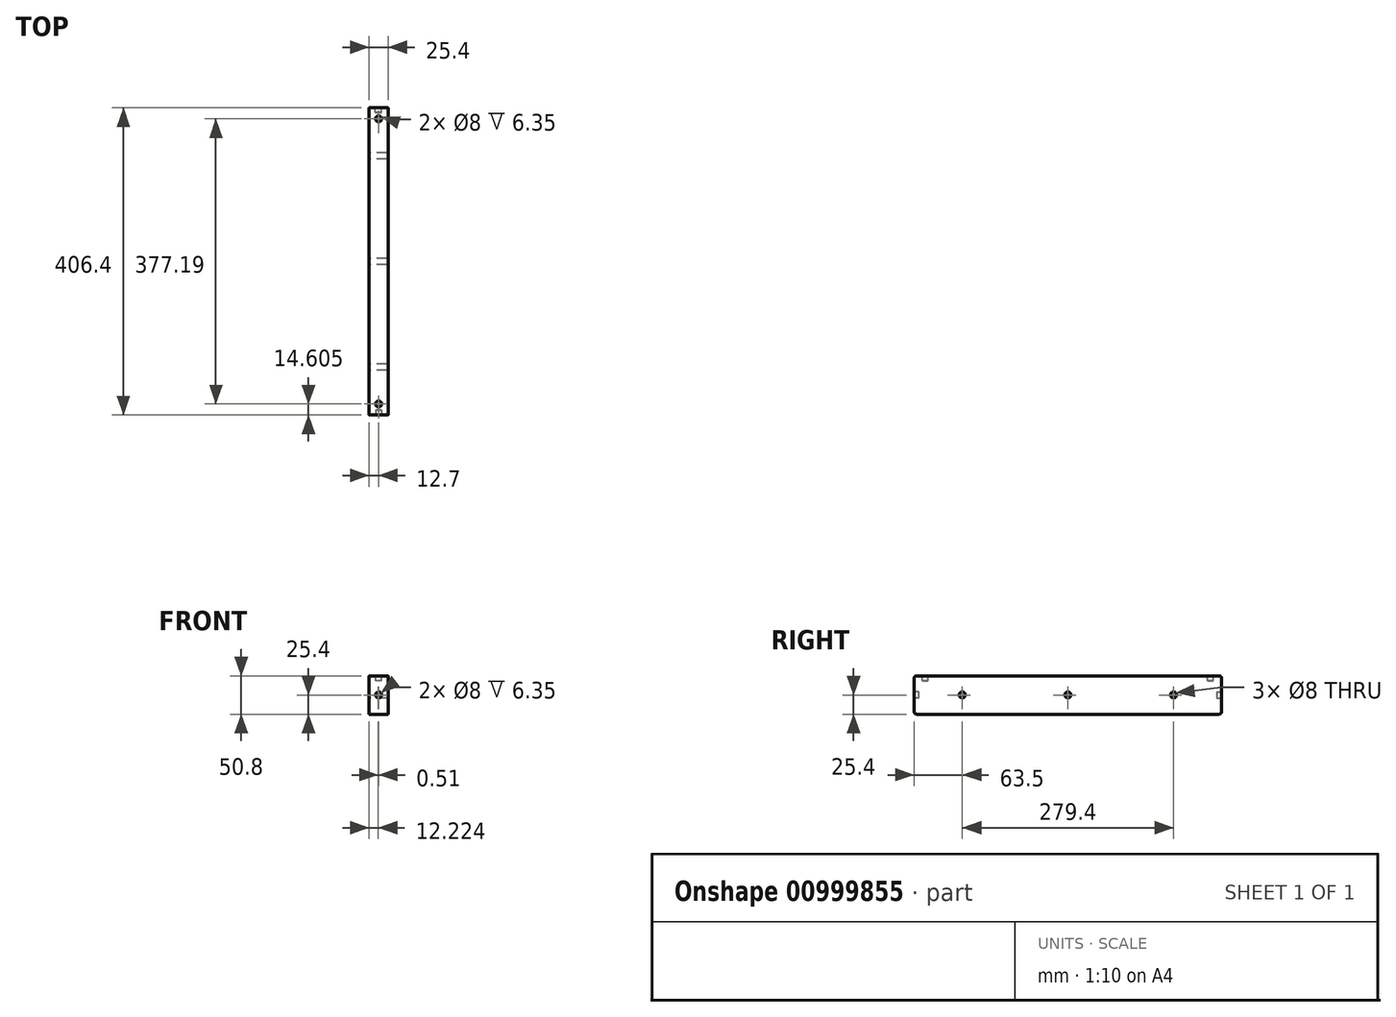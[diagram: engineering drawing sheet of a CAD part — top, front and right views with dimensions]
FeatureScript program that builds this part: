
annotation { "Feature Type Name" : "Feature", "Feature Type Description" : "" }
export const myFeature = defineFeature(function(context is Context, id is Id, definition is map)
    precondition{}
    {
        {
            var Q0;
            Q0=qCreatedBy(makeId("Right.planeOp"),FACE);
            var sketch = newSketch(context, id + "F0", { "sketchPlane" : qUnion([Q0])});
            skLineSegment(sketch, "E0.bottom", {"start": v(200.03, 25.4) * mm, "end": v(-200.03, 25.4) * mm});
            skLineSegment(sketch, "E0.top", {"start": v(200.03, -25.4) * mm, "end": v(-200.03, -25.4) * mm});
            skLineSegment(sketch, "E0.left", {"start": v(203.2, 22.23) * mm, "end": v(203.2, -22.23) * mm});
            skLineSegment(sketch, "E0.right", {"start": v(-203.2, 22.22) * mm, "end": v(-203.2, -22.23) * mm});
            skPoint(sketch, "E0.middle", {"position": v(0, 0) * mm});
            skPoint(sketch, "E1.visualSharp", {"position": v(-203.2, 25.4) * mm});
            skArc(sketch, "E1.filletArc", {"start": v(-200.03, 25.4) * mm, "mid": v(-202.27, 24.47) * mm, "end": v(-203.2, 22.22) * mm});
            skPoint(sketch, "E2.visualSharp", {"position": v(-203.2, -25.4) * mm});
            skArc(sketch, "E2.filletArc", {"start": v(-203.2, -22.23) * mm, "mid": v(-202.27, -24.47) * mm, "end": v(-200.03, -25.4) * mm});
            skPoint(sketch, "E3.visualSharp", {"position": v(203.2, 25.4) * mm});
            skArc(sketch, "E3.filletArc", {"start": v(203.2, 22.23) * mm, "mid": v(202.27, 24.47) * mm, "end": v(200.03, 25.4) * mm});
            skPoint(sketch, "E4.visualSharp", {"position": v(203.2, -25.4) * mm});
            skArc(sketch, "E4.filletArc", {"start": v(200.03, -25.4) * mm, "mid": v(202.27, -24.47) * mm, "end": v(203.2, -22.23) * mm});
            skCircle(sketch, "E5", {"center": v(0, 0) * mm, "radius": 4 * mm});
            skCircle(sketch, "E6", {"center": v(-139.7, 0) * mm, "radius": 4 * mm});
            skCircle(sketch, "E7", {"center": v(139.7, 0) * mm, "radius": 4 * mm});
            skSolve(sketch);
        }
        {
            var Q0;
            Q0=makeQuery(id+"F0.imprint","IMPRINT",FACE,{"disambiguationData":[TD([[makeQuery(id+"F0.imprint","IMPRINT",EDGE,{"derivedFrom":sQuery(id+"F0.wireOp",EDGE,"E0.bottom")}),1.0]])]});
            extrude(context, id + "F1", {"entities" : qUnion([Q0]), "depth" : 25.4 * mm, "offsetDistance" : 25.4 * mm});
        }
        {
            var Q0;
            Q0=makeQuery(id+"F1.opExtrude","SWEPT_FACE",FACE,{"disambiguationData":[OSD([sQuery(id+"F0.wireOp",EDGE,"E0.right")])]});
            var sketch = newSketch(context, id + "F2", { "sketchPlane" : qUnion([Q0])});
            skPoint(sketch, "E8.endSnap0", {"position": v(25.4, 0) * mm});
            skCircle(sketch, "E9", {"center": v(12.73, 0) * mm, "radius": 4 * mm});
            skSolve(sketch);
        }
        {
            var Q0;
            Q0=makeQuery(id+"F2.imprint","IMPRINT",FACE,{"disambiguationData":[TD([[makeQuery(id+"F2.imprint","IMPRINT",EDGE,{"derivedFrom":sQuery(id+"F2.wireOp",EDGE,"E9")}),1.0]])]});
            extrude(context, id + "F3", {"entities" : qUnion([Q0]), "operationType" : NewBodyOperationType.REMOVE, "oppositeDirection" : true, "depth" : 6.35 * mm, "offsetDistance" : 25.4 * mm});
        }
        {
            var Q0;
            Q0=makeQuery(id+"F1.opExtrude","SWEPT_FACE",FACE,{"disambiguationData":[OSD([sQuery(id+"F0.wireOp",EDGE,"E0.left")])]});
            var sketch = newSketch(context, id + "F4", { "sketchPlane" : qUnion([Q0])});
            skCircle(sketch, "E10", {"center": v(-12.22, 0) * mm, "radius": 4 * mm});
            skSolve(sketch);
        }
        {
            var Q0;
            Q0=makeQuery(id+"F4.imprint","IMPRINT",FACE,{"disambiguationData":[TD([[makeQuery(id+"F4.imprint","IMPRINT",EDGE,{"derivedFrom":sQuery(id+"F4.wireOp",EDGE,"E10")}),1.0]])]});
            extrude(context, id + "F5", {"entities" : qUnion([Q0]), "operationType" : NewBodyOperationType.REMOVE, "oppositeDirection" : true, "depth" : 6.35 * mm, "offsetDistance" : 25.4 * mm});
        }
        {
            var Q0;
            Q0=makeQuery(id+"F1.opExtrude","SWEPT_FACE",FACE,{"disambiguationData":[OSD([sQuery(id+"F0.wireOp",EDGE,"E0.bottom")])]});
            var sketch = newSketch(context, id + "F6", { "sketchPlane" : qUnion([Q0])});
            skCircle(sketch, "E11", {"center": v(12.7, -188.6) * mm, "radius": 4 * mm});
            skSolve(sketch);
        }
        {
            var Q0;
            Q0=makeQuery(id+"F6.imprint","IMPRINT",FACE,{"disambiguationData":[TD([[makeQuery(id+"F6.imprint","IMPRINT",EDGE,{"derivedFrom":sQuery(id+"F6.wireOp",EDGE,"E11")}),1.0]])]});
            extrude(context, id + "F7", {"entities" : qUnion([Q0]), "operationType" : NewBodyOperationType.REMOVE, "oppositeDirection" : true, "depth" : 6.35 * mm, "offsetDistance" : 25.4 * mm});
        }
        {
            var Q0;
            Q0=makeQuery(id+"F1.opExtrude","SWEPT_FACE",FACE,{"disambiguationData":[OSD([sQuery(id+"F0.wireOp",EDGE,"E0.bottom")])]});
            var sketch = newSketch(context, id + "F8", { "sketchPlane" : qUnion([Q0])});
            skPoint(sketch, "E12.endSnap0", {"position": v(12.7, 200.03) * mm});
            skCircle(sketch, "E13", {"center": v(12.7, 188.6) * mm, "radius": 4 * mm});
            skSolve(sketch);
        }
        {
            var Q0;
            Q0=makeQuery(id+"F8.imprint","IMPRINT",FACE,{"disambiguationData":[TD([[makeQuery(id+"F8.imprint","IMPRINT",EDGE,{"derivedFrom":sQuery(id+"F8.wireOp",EDGE,"E13")}),1.0]])]});
            extrude(context, id + "F9", {"entities" : qUnion([Q0]), "operationType" : NewBodyOperationType.REMOVE, "oppositeDirection" : true, "depth" : 6.35 * mm, "offsetDistance" : 25.4 * mm});
        }
    });
